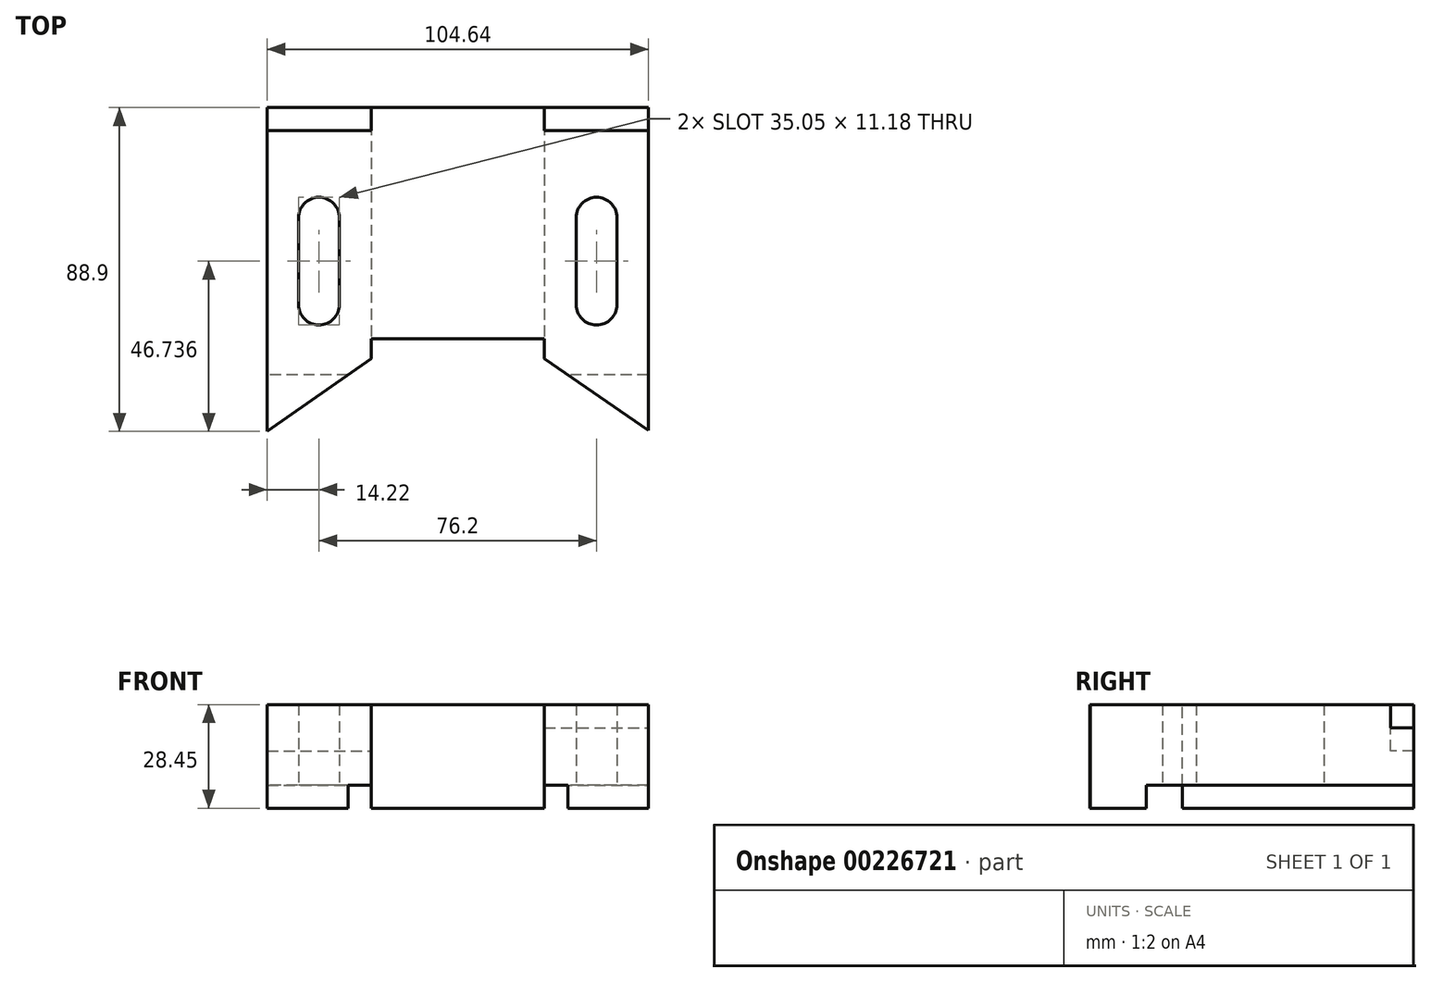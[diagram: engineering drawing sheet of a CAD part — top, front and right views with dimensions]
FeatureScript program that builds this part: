
annotation { "Feature Type Name" : "Feature", "Feature Type Description" : "" }
export const myFeature = defineFeature(function(context is Context, id is Id, definition is map)
    precondition{}
    {
        {
            var Q0;
            Q0=qCreatedBy(makeId("Top.planeOp"),FACE);
            var sketch = newSketch(context, id + "F0", { "sketchPlane" : qUnion([Q0])});
            skLineSegment(sketch, "E0.bottom", {"start": v(-52.32, 44.45) * mm, "end": v(52.32, 44.45) * mm});
            skLineSegment(sketch, "E0.top", {"start": v(-52.32, -44.45) * mm, "end": v(52.32, -44.45) * mm});
            skLineSegment(sketch, "E0.left", {"start": v(-52.32, 44.45) * mm, "end": v(-52.32, -44.45) * mm});
            skLineSegment(sketch, "E0.right", {"start": v(52.32, 44.45) * mm, "end": v(52.32, -44.45) * mm});
            skPoint(sketch, "E0.middle", {"position": v(0, 0) * mm});
            skLineSegment(sketch, "E1", {"start": v(-23.75, 44.45) * mm, "end": v(-23.75, -44.45) * mm});
            skLineSegment(sketch, "E2", {"start": v(23.75, 44.45) * mm, "end": v(23.75, -44.45) * mm});
            skCircle(sketch, "E3", {"center": v(-38.1, 14.22) * mm, "radius": 5.59 * mm});
            skCircle(sketch, "E4", {"center": v(-38.1, -9.65) * mm, "radius": 5.59 * mm});
            skCircle(sketch, "E5", {"center": v(38.1, 14.22) * mm, "radius": 5.59 * mm});
            skCircle(sketch, "E6", {"center": v(38.1, -9.65) * mm, "radius": 5.59 * mm});
            skLineSegment(sketch, "E7", {"start": v(-43.69, 14.22) * mm, "end": v(-43.69, -9.65) * mm});
            skLineSegment(sketch, "E8", {"start": v(-32.51, 14.22) * mm, "end": v(-32.51, -9.65) * mm});
            skLineSegment(sketch, "E9", {"start": v(-38.1, -9.65) * mm, "end": v(-38.1, 14.22) * mm, "construction": true});
            skLineSegment(sketch, "E10", {"start": v(43.69, 14.22) * mm, "end": v(43.69, -9.65) * mm});
            skLineSegment(sketch, "E11", {"start": v(32.51, 14.22) * mm, "end": v(32.51, -9.65) * mm});
            skLineSegment(sketch, "E12", {"start": v(38.1, 14.22) * mm, "end": v(38.1, -9.65) * mm, "construction": true});
            skSolve(sketch);
        }
        {
            var Q0;
            Q0 = qSketchRegion(id + "F0", true);
            extrude(context, id + "F1", {"entities" : qUnion([Q0]), "depth" : 28.45 * mm});
        }
        {
            var Q0;
            Q0 = qSketchRegion(id + "F0", true);
            extrude(context, id + "F2", {"entities" : qUnion([Q0]), "operationType" : NewBodyOperationType.ADD, "depth" : 25.4 * mm});
        }
        {
            var Q0;
            Q0=makeQuery(id+"F1.opExtrude","CAP_FACE",FACE,{"disambiguationData":[OSD([sQuery(id+"F0.wireOp",EDGE,"E0.bottom"),sQuery(id+"F0.wireOp",EDGE,"E0.top"),sQuery(id+"F0.wireOp",EDGE,"E0.left"),sQuery(id+"F0.wireOp",EDGE,"E0.right"),sQuery(id+"F0.wireOp",EDGE,"E3"),sQuery(id+"F0.wireOp",EDGE,"E4"),sQuery(id+"F0.wireOp",EDGE,"E5"),sQuery(id+"F0.wireOp",EDGE,"E6"),sQuery(id+"F0.wireOp",EDGE,"E7"),sQuery(id+"F0.wireOp",EDGE,"E8"),sQuery(id+"F0.wireOp",EDGE,"E10"),sQuery(id+"F0.wireOp",EDGE,"E11")])],"isStart":true});
            var sketch = newSketch(context, id + "F3", { "sketchPlane" : qUnion([Q0])});
            skLineSegment(sketch, "E13", {"start": v(52.32, -44.45) * mm, "end": v(23.75, -44.45) * mm});
            skLineSegment(sketch, "E14", {"start": v(23.75, -44.45) * mm, "end": v(23.75, 28.96) * mm});
            skLineSegment(sketch, "E15", {"start": v(52.32, 28.96) * mm, "end": v(52.32, -44.45) * mm});
            skLineSegment(sketch, "E16", {"start": v(52.32, 28.96) * mm, "end": v(23.75, 28.96) * mm});
            skPoint(sketch, "E17.orphan", {"position": v(23.75, 44.45) * mm});
            skLineSegment(sketch, "E18", {"start": v(-52.32, -44.45) * mm, "end": v(-23.75, -44.45) * mm});
            skLineSegment(sketch, "E19", {"start": v(-23.75, -44.45) * mm, "end": v(-23.75, 28.96) * mm});
            skLineSegment(sketch, "E20", {"start": v(-23.75, 28.96) * mm, "end": v(-52.32, 28.96) * mm});
            skLineSegment(sketch, "E21", {"start": v(-52.32, 28.96) * mm, "end": v(-52.32, -44.45) * mm});
            skSolve(sketch);
        }
        {
            var Q0;
            Q0=makeQuery(id+"F3.imprint","IMPRINT",FACE,{"disambiguationData":[TD([[makeQuery(id+"F3.imprint","IMPRINT",EDGE,{"derivedFrom":sQuery(id+"F3.wireOp",EDGE,"E13")}),1.0]])]});
            var Q1;
            Q1=makeQuery(id+"F3.imprint","IMPRINT",FACE,{"disambiguationData":[TD([[makeQuery(id+"F3.imprint","IMPRINT",EDGE,{"derivedFrom":sQuery(id+"F3.wireOp",EDGE,"E18")}),1.0]])]});
            extrude(context, id + "F4", {"entities" : qUnion([Q0, Q1]), "operationType" : NewBodyOperationType.REMOVE, "oppositeDirection" : true, "depth" : 6.35 * mm});
        }
        {
            var Q0;
            Q0=makeQuery(id+"F1.opExtrude","CAP_FACE",FACE,{"disambiguationData":[OSD([sQuery(id+"F0.wireOp",EDGE,"E0.bottom"),sQuery(id+"F0.wireOp",EDGE,"E0.top"),sQuery(id+"F0.wireOp",EDGE,"E0.left"),sQuery(id+"F0.wireOp",EDGE,"E0.right"),sQuery(id+"F0.wireOp",EDGE,"E3"),sQuery(id+"F0.wireOp",EDGE,"E4"),sQuery(id+"F0.wireOp",EDGE,"E5"),sQuery(id+"F0.wireOp",EDGE,"E6"),sQuery(id+"F0.wireOp",EDGE,"E7"),sQuery(id+"F0.wireOp",EDGE,"E8"),sQuery(id+"F0.wireOp",EDGE,"E10"),sQuery(id+"F0.wireOp",EDGE,"E11")])],"isStart":false});
            var sketch = newSketch(context, id + "F5", { "sketchPlane" : qUnion([Q0])});
            skLineSegment(sketch, "E22", {"start": v(-52.32, 44.45) * mm, "end": v(-23.75, 44.45) * mm});
            skLineSegment(sketch, "E23", {"start": v(-23.75, 44.45) * mm, "end": v(-23.75, -44.45) * mm});
            skLineSegment(sketch, "E24", {"start": v(-23.75, -44.45) * mm, "end": v(-34.8, -44.45) * mm});
            skLineSegment(sketch, "E25", {"start": v(-34.8, -44.45) * mm, "end": v(-34.8, -25.15) * mm});
            skLineSegment(sketch, "E26", {"start": v(-34.8, -25.15) * mm, "end": v(-52.32, -25.15) * mm});
            skLineSegment(sketch, "E27", {"start": v(-52.32, -25.15) * mm, "end": v(-52.32, 44.45) * mm});
            skLineSegment(sketch, "E28", {"start": v(52.32, 44.45) * mm, "end": v(23.75, 44.45) * mm});
            skLineSegment(sketch, "E29", {"start": v(23.75, 44.45) * mm, "end": v(23.75, -44.45) * mm});
            skLineSegment(sketch, "E30", {"start": v(23.75, -44.45) * mm, "end": v(34.8, -44.45) * mm});
            skLineSegment(sketch, "E31", {"start": v(34.8, -44.45) * mm, "end": v(34.8, -25.15) * mm});
            skLineSegment(sketch, "E32", {"start": v(34.8, -25.15) * mm, "end": v(52.32, -25.15) * mm});
            skLineSegment(sketch, "E33", {"start": v(52.32, -25.15) * mm, "end": v(52.32, 44.45) * mm});
            skLineSegment(sketch, "E34", {"start": v(-52.32, 44.45) * mm, "end": v(-52.32, 38.1) * mm});
            skLineSegment(sketch, "E35", {"start": v(-52.32, 38.1) * mm, "end": v(-23.75, 38.1) * mm});
            skLineSegment(sketch, "E36", {"start": v(-23.75, 38.1) * mm, "end": v(-23.75, 44.45) * mm});
            skLineSegment(sketch, "E37", {"start": v(23.75, 44.45) * mm, "end": v(52.32, 44.45) * mm});
            skLineSegment(sketch, "E38", {"start": v(52.32, 38.1) * mm, "end": v(23.75, 38.1) * mm});
            skLineSegment(sketch, "E39", {"start": v(23.75, 38.1) * mm, "end": v(23.75, 44.45) * mm});
            skSolve(sketch);
        }
        {
            var Q0;
            Q0=makeQuery(id+"F5.imprint","IMPRINT",FACE,{"disambiguationData":[TD([[makeQuery(id+"F5.imprint","IMPRINT",EDGE,{"derivedFrom":sQuery(id+"F5.wireOp",EDGE,"E28")}),-1.0]])]});
            var Q1;
            Q1=makeQuery(id+"F5.imprint","IMPRINT",FACE,{"disambiguationData":[TD([[makeQuery(id+"F5.imprint","IMPRINT",EDGE,{"derivedFrom":sQuery(id+"F5.wireOp",EDGE,"E23")}),-1.0]])]});
            var Q2;
            Q2=makeQuery(id+"F5.imprint","IMPRINT",FACE,{"disambiguationData":[TD([[makeQuery(id+"F5.imprint","IMPRINT",EDGE,{"derivedFrom":sQuery(id+"F5.wireOp",EDGE,"E22")}),-1.0]])]});
            var Q3;
            Q3=makeQuery(id+"F5.imprint","IMPRINT",FACE,{"disambiguationData":[TD([[makeQuery(id+"F5.imprint","IMPRINT",EDGE,{"derivedFrom":sQuery(id+"F5.wireOp",EDGE,"E29")}),1.0]])]});
            extrude(context, id + "F6", {"entities" : qUnion([Q0, Q1, Q2, Q3]), "operationType" : NewBodyOperationType.REMOVE, "oppositeDirection" : true, "depth" : 6.35 * mm});
        }
        {
            var Q0;
            Q0=makeQuery(id+"F5.imprint","IMPRINT",FACE,{"disambiguationData":[TD([[makeQuery(id+"F5.imprint","IMPRINT",EDGE,{"derivedFrom":sQuery(id+"F5.wireOp",EDGE,"E22")}),-1.0]])]});
            var Q1;
            {var subQ0=sQuery(id+"F5.wireOp",EDGE,"E37");Q1=makeQuery(id+"F5.imprint","IMPRINT",FACE,{"disambiguationData":[TD([[makeQuery(id+"F5.imprint","IMPRINT",EDGE,{"derivedFrom":subQ0}),-1.0]])]});}
            extrude(context, id + "F7", {"entities" : qUnion([Q0, Q1]), "operationType" : NewBodyOperationType.REMOVE, "oppositeDirection" : true, "depth" : 12.7 * mm});
        }
        {
            var Q0;
            {var subQ0=sQuery(id+"F0.wireOp",EDGE,"E0.right");var subQ1=sQuery(id+"F0.wireOp",EDGE,"E0.top");var subQ2=sQuery(id+"F0.wireOp",EDGE,"E0.bottom");Q0=makeQuery(id+"F6.boolean.opBoolean","SPLIT",FACE,{"disambiguationData":[TD([makeQuery(id+"F1.opExtrude","SWEPT_FACE",FACE,{"disambiguationData":[OSD([subQ2])]})])],"derivedFrom":makeQuery(id+"F1.opExtrude","CAP_FACE",FACE,{"disambiguationData":[OSD([subQ2,subQ1,sQuery(id+"F0.wireOp",EDGE,"E0.left"),subQ0,sQuery(id+"F0.wireOp",EDGE,"E3"),sQuery(id+"F0.wireOp",EDGE,"E4"),sQuery(id+"F0.wireOp",EDGE,"E5"),sQuery(id+"F0.wireOp",EDGE,"E6"),sQuery(id+"F0.wireOp",EDGE,"E7"),sQuery(id+"F0.wireOp",EDGE,"E8"),sQuery(id+"F0.wireOp",EDGE,"E10"),sQuery(id+"F0.wireOp",EDGE,"E11")])],"isStart":false})});}
            var sketch = newSketch(context, id + "F8", { "sketchPlane" : qUnion([Q0])});
            skLineSegment(sketch, "E40.bottom", {"start": v(-23.75, -44.45) * mm, "end": v(23.75, -44.45) * mm});
            skLineSegment(sketch, "E40.top", {"start": v(-23.75, -19.05) * mm, "end": v(23.75, -19.05) * mm});
            skLineSegment(sketch, "E40.left", {"start": v(-23.75, -44.45) * mm, "end": v(-23.75, -19.05) * mm});
            skLineSegment(sketch, "E40.right", {"start": v(23.75, -44.45) * mm, "end": v(23.75, -19.05) * mm});
            skSolve(sketch);
        }
        {
            var Q0;
            Q0 = qSketchRegion(id + "F8", true);
            extrude(context, id + "F9", {"entities" : qUnion([Q0]), "operationType" : NewBodyOperationType.REMOVE, "endBound" : BoundingType.THROUGH_ALL, "oppositeDirection" : true, "depth" : 25.4 * mm});
        }
        {
            var Q0;
            {var subQ1=sQuery(id+"F0.wireOp",EDGE,"E0.left");Q0=makeQuery(id+"F0.imprint","IMPRINT",FACE,{"disambiguationData":[TD([[makeQuery(id+"F0.imprint","IMPRINT",EDGE,{"derivedFrom":subQ1}),1.0]])]});}
            var sketch = newSketch(context, id + "F10", { "sketchPlane" : qUnion([Q0])});
            skLineSegment(sketch, "E41", {"start": v(-52.32, -44.45) * mm, "end": v(-23.75, -24.5) * mm});
            skLineSegment(sketch, "E42", {"start": v(-52.32, -44.45) * mm, "end": v(-23.75, -44.45) * mm});
            skLineSegment(sketch, "E43", {"start": v(-23.75, -44.45) * mm, "end": v(-23.75, -24.5) * mm});
            skLineSegment(sketch, "E44", {"start": v(52.67, -44.45) * mm, "end": v(23.75, -24.5) * mm});
            skLineSegment(sketch, "E45", {"start": v(23.75, -24.5) * mm, "end": v(23.75, -44.45) * mm});
            skLineSegment(sketch, "E46", {"start": v(52.67, -44.45) * mm, "end": v(23.75, -44.45) * mm});
            skSolve(sketch);
        }
        {
            var Q0;
            Q0 = qSketchRegion(id + "F10", true);
            extrude(context, id + "F11", {"entities" : qUnion([Q0]), "operationType" : NewBodyOperationType.REMOVE, "endBound" : BoundingType.THROUGH_ALL, "depth" : 25.4 * mm});
        }
    });
